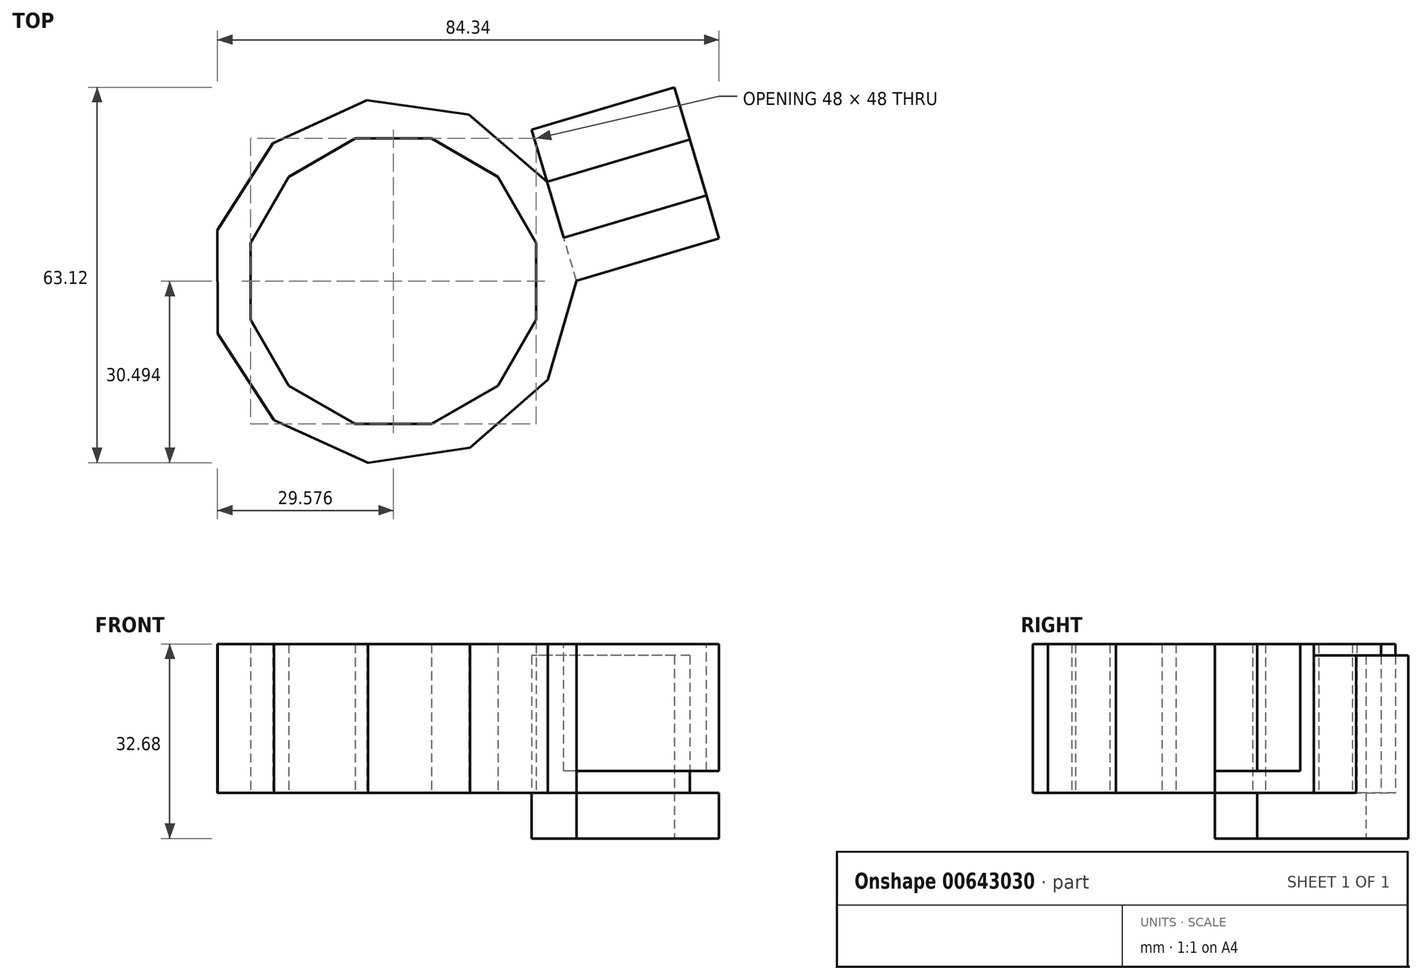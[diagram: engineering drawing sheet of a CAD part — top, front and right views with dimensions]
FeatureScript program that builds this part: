
annotation { "Feature Type Name" : "Feature", "Feature Type Description" : "" }
export const myFeature = defineFeature(function(context is Context, id is Id, definition is map)
    precondition{}
    {
        {
            var Q0;
            Q0=qCreatedBy(makeId("Top.planeOp"),FACE);
            var sketch = newSketch(context, id + "F0", { "sketchPlane" : qUnion([Q0])});
            skCircle(sketch, "E0.cCircle", {"center": v(-8.1, -21) * mm, "radius": 29.55 * mm, "construction": true});
            skLineSegment(sketch, "E0.0", {"start": v(17.76, -4.28) * mm, "end": v(22.7, -20.91) * mm});
            skLineSegment(sketch, "E0.1", {"start": v(22.7, -20.91) * mm, "end": v(17.87, -37.58) * mm});
            skLineSegment(sketch, "E0.2", {"start": v(17.87, -37.58) * mm, "end": v(4.79, -48.98) * mm});
            skLineSegment(sketch, "E0.3", {"start": v(4.79, -48.98) * mm, "end": v(-12.38, -51.5) * mm});
            skLineSegment(sketch, "E0.4", {"start": v(-12.38, -51.5) * mm, "end": v(-28.19, -44.34) * mm});
            skLineSegment(sketch, "E0.5", {"start": v(-28.19, -44.34) * mm, "end": v(-37.62, -29.77) * mm});
            skLineSegment(sketch, "E0.6", {"start": v(-37.62, -29.77) * mm, "end": v(-37.67, -12.42) * mm});
            skLineSegment(sketch, "E0.7", {"start": v(-37.67, -12.42) * mm, "end": v(-28.33, 2.2) * mm});
            skLineSegment(sketch, "E0.8", {"start": v(-28.33, 2.2) * mm, "end": v(-12.57, 9.46) * mm});
            skLineSegment(sketch, "E0.9", {"start": v(-12.57, 9.46) * mm, "end": v(4.61, 7.05) * mm});
            skLineSegment(sketch, "E0.10", {"start": v(4.61, 7.05) * mm, "end": v(17.76, -4.28) * mm});
            skPoint(sketch, "E0.0.midPoint", {"position": v(20.23, -12.6) * mm});
            skCircle(sketch, "E1.cCircle", {"center": v(-8.1, -21) * mm, "radius": 24 * mm, "construction": true});
            skLineSegment(sketch, "E1.0", {"start": v(-1.66, -45) * mm, "end": v(-14.52, -45) * mm});
            skLineSegment(sketch, "E1.1", {"start": v(-14.52, -45) * mm, "end": v(-25.66, -38.58) * mm});
            skLineSegment(sketch, "E1.2", {"start": v(-25.66, -38.58) * mm, "end": v(-32.1, -27.44) * mm});
            skLineSegment(sketch, "E1.3", {"start": v(-32.1, -27.44) * mm, "end": v(-32.1, -14.58) * mm});
            skLineSegment(sketch, "E1.4", {"start": v(-32.1, -14.58) * mm, "end": v(-25.66, -3.44) * mm});
            skLineSegment(sketch, "E1.5", {"start": v(-25.66, -3.44) * mm, "end": v(-14.52, 3) * mm});
            skLineSegment(sketch, "E1.6", {"start": v(-14.52, 3) * mm, "end": v(-1.66, 3) * mm});
            skLineSegment(sketch, "E1.7", {"start": v(-1.66, 3) * mm, "end": v(9.48, -3.44) * mm});
            skLineSegment(sketch, "E1.8", {"start": v(9.48, -3.44) * mm, "end": v(15.9, -14.58) * mm});
            skLineSegment(sketch, "E1.9", {"start": v(15.9, -14.58) * mm, "end": v(15.9, -27.44) * mm});
            skLineSegment(sketch, "E1.10", {"start": v(15.9, -27.44) * mm, "end": v(9.48, -38.58) * mm});
            skLineSegment(sketch, "E1.11", {"start": v(9.48, -38.58) * mm, "end": v(-1.66, -45) * mm});
            skPoint(sketch, "E1.0.midPoint", {"position": v(-8.1, -45) * mm});
            skSolve(sketch);
        }
        {
            var Q0;
            Q0=makeQuery(id+"F0.imprint","IMPRINT",FACE,{"disambiguationData":[TD([[makeQuery(id+"F0.imprint","IMPRINT",EDGE,{"derivedFrom":sQuery(id+"F0.wireOp",EDGE,"E0.0")}),-1.0]])]});
            extrude(context, id + "F1", {"entities" : qUnion([Q0]), "depth" : 25 * mm, "offsetDistance" : 25 * mm});
        }
        {
            var Q0;
            Q0=makeQuery(id+"F1.opExtrude","SWEPT_FACE",FACE,{"disambiguationData":[OSD([sQuery(id+"F0.wireOp",EDGE,"E0.0")])]});
            var sketch = newSketch(context, id + "F2", { "sketchPlane" : qUnion([Q0])});
            skLineSegment(sketch, "E2.bottom", {"start": v(-26.5, 23.08) * mm, "end": v(0, 23.08) * mm});
            skLineSegment(sketch, "E2.top", {"start": v(-26.5, -7.68) * mm, "end": v(0, -7.68) * mm});
            skLineSegment(sketch, "E2.left", {"start": v(-26.5, 23.08) * mm, "end": v(-26.5, -7.68) * mm});
            skLineSegment(sketch, "E2.right", {"start": v(0, 23.08) * mm, "end": v(0, -7.68) * mm});
            skLineSegment(sketch, "E3.bottom", {"start": v(-26.5, 12.5) * mm, "end": v(-42.55, 12.5) * mm});
            skLineSegment(sketch, "E3.top", {"start": v(-26.5, -9.54) * mm, "end": v(-42.55, -9.54) * mm});
            skLineSegment(sketch, "E3.left", {"start": v(-26.5, 12.5) * mm, "end": v(-26.5, -9.54) * mm});
            skLineSegment(sketch, "E3.right", {"start": v(-42.55, 12.5) * mm, "end": v(-42.55, -9.54) * mm});
            skLineSegment(sketch, "E4.bottom", {"start": v(-38.07, 3.68) * mm, "end": v(-18.98, 3.68) * mm});
            skLineSegment(sketch, "E4.top", {"start": v(-38.07, 38.99) * mm, "end": v(-18.98, 38.99) * mm});
            skLineSegment(sketch, "E4.left", {"start": v(-38.07, 3.68) * mm, "end": v(-38.07, 38.99) * mm});
            skLineSegment(sketch, "E4.right", {"start": v(-18.98, 3.68) * mm, "end": v(-18.98, 38.99) * mm});
            skSolve(sketch);
        }
        {
            var Q0;
            {var subQ1=sQuery(id+"F2.wireOp",EDGE,"E2.left");Q0=makeQuery(id+"F2.imprint","IMPRINT",FACE,{"disambiguationData":[TD([[makeQuery(id+"F2.imprint","IMPRINT",EDGE,{"derivedFrom":subQ1}),1.0]])]});}
            var Q1;
            {var subQ3=sQuery(id+"F2.wireOp",EDGE,"E2.top");Q1=makeQuery(id+"F2.imprint","IMPRINT",FACE,{"disambiguationData":[TD([[makeQuery(id+"F2.imprint","IMPRINT",EDGE,{"derivedFrom":subQ3}),1.0]])]});}
            var Q2;
            {var subQ0=sQuery(id+"F2.wireOp",EDGE,"E2.bottom");var subQ4=sQuery(id+"F2.wireOp",EDGE,"E4.right");var subQ5=makeQuery(id+"F2.imprint","INTERSECT",VERTEX,{"derivedFrom":[subQ0,subQ4]});Q2=makeQuery(id+"F2.imprint","IMPRINT",FACE,{"disambiguationData":[TD([[makeQuery(id+"F2.imprint","IMPRINT",EDGE,{"disambiguationData":[TD([[subQ5,-1.0]])],"derivedFrom":subQ4}),1.0]])]});}
            extrude(context, id + "F3", {"entities" : qUnion([Q0, Q1, Q2]), "operationType" : NewBodyOperationType.ADD, "depth" : 25 * mm, "offsetDistance" : 25 * mm});
        }
    });
